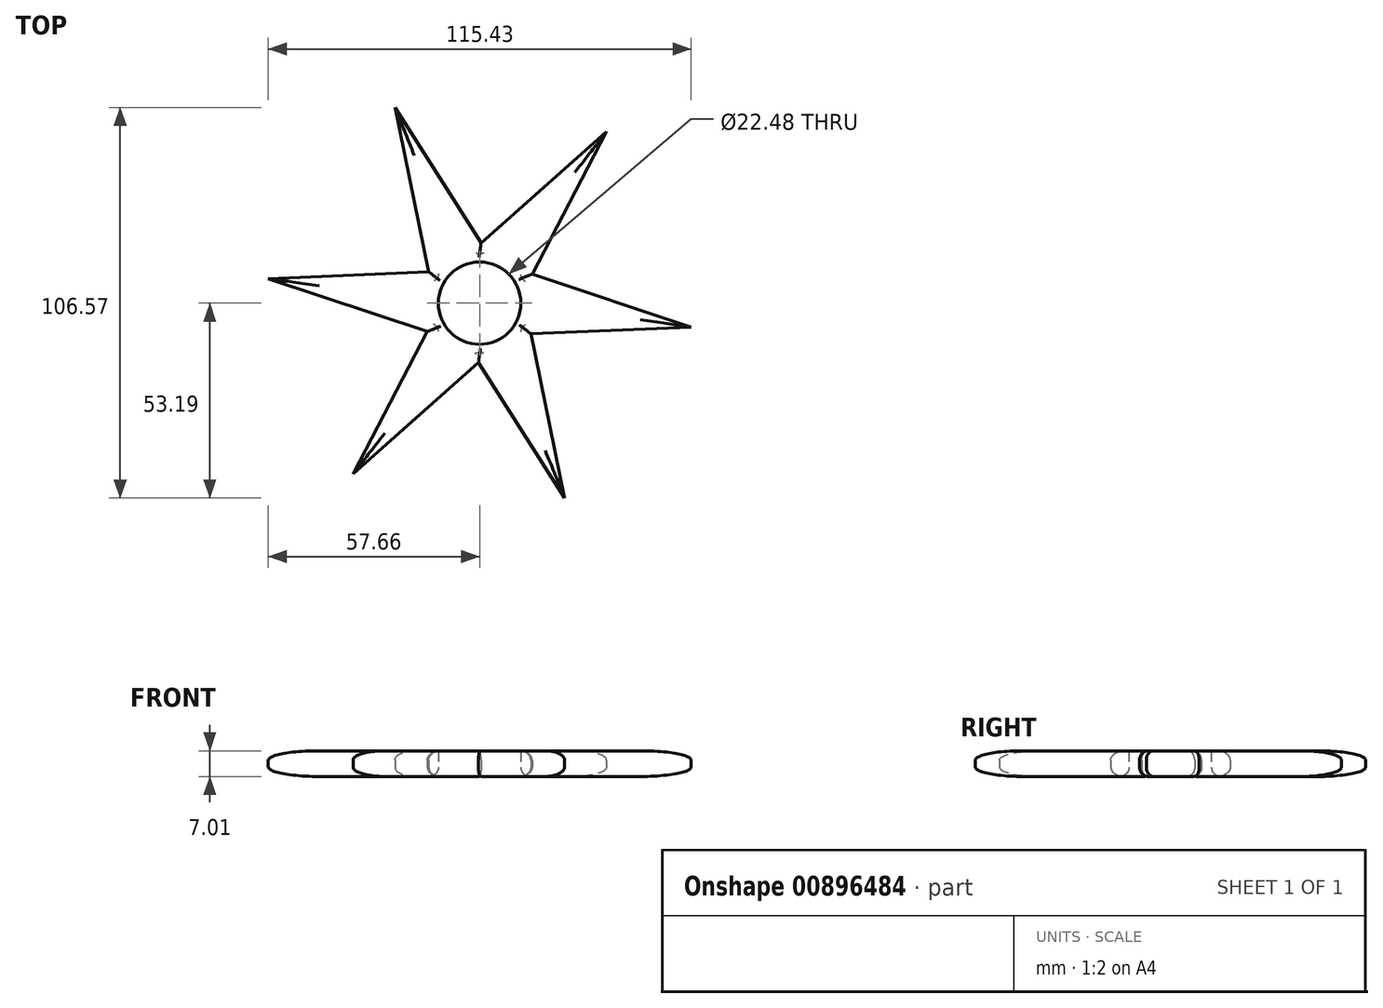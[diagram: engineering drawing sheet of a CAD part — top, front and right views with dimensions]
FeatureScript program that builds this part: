
annotation { "Feature Type Name" : "Feature", "Feature Type Description" : "" }
export const myFeature = defineFeature(function(context is Context, id is Id, definition is map)
    precondition{}
    {
        {
            var Q0;
            Q0=qCreatedBy(makeId("Top.planeOp"),FACE);
            var sketch = newSketch(context, id + "F0", { "sketchPlane" : qUnion([Q0])});
            skCircle(sketch, "E0", {"center": v(0, 0) * mm, "radius": 11.24 * mm});
            skCircle(sketch, "E1", {"center": v(0, 0) * mm, "radius": 16.04 * mm});
            skLineSegment(sketch, "E2", {"start": v(0, 16.04) * mm, "end": v(34.64, 46.77) * mm});
            skLineSegment(sketch, "E3", {"start": v(34.64, 46.77) * mm, "end": v(14.15, 7.54) * mm});
            skLineSegment(sketch, "E4.1.0", {"start": v(-23.08, 53.38) * mm, "end": v(0.66, 16.03) * mm});
            skLineSegment(sketch, "E4.1.1", {"start": v(-13.78, 8.02) * mm, "end": v(-23.08, 53.38) * mm});
            skLineSegment(sketch, "E4.2.0", {"start": v(-57.66, 6.7) * mm, "end": v(-13.44, 8.58) * mm});
            skLineSegment(sketch, "E4.2.1", {"start": v(-13.72, -7.92) * mm, "end": v(-57.66, 6.7) * mm});
            skPoint(sketch, "E4.center", {"position": v(0.05, 0.1) * mm});
            skLineSegment(sketch, "E5.2.3.0", {"start": v(-34.53, -46.58) * mm, "end": v(-14.04, -7.35) * mm});
            skLineSegment(sketch, "E5.3.3.0", {"start": v(0.1, -15.85) * mm, "end": v(-34.53, -46.58) * mm});
            skLineSegment(sketch, "E5.2.4.0", {"start": v(23.2, -53.2) * mm, "end": v(-0.55, -15.84) * mm});
            skLineSegment(sketch, "E5.3.4.0", {"start": v(13.89, -7.83) * mm, "end": v(23.2, -53.2) * mm});
            skLineSegment(sketch, "E5.2.5.0", {"start": v(57.77, -6.51) * mm, "end": v(13.55, -8.4) * mm});
            skLineSegment(sketch, "E5.3.5.0", {"start": v(13.83, 8.11) * mm, "end": v(57.77, -6.51) * mm});
            skSolve(sketch);
        }
        {
            var Q0;
            Q0 = qSketchRegion(id + "F0", true);
            var Q1;
            Q1=makeQuery(id+"F0.imprint","IMPRINT",FACE,{"disambiguationData":[TD([[makeQuery(id+"F0.imprint","IMPRINT",EDGE,{"derivedFrom":sQuery(id+"F0.wireOp",EDGE,"E0")}),-1.0]])]});
            extrude(context, id + "F1", {"entities" : qUnion([Q0, Q1]), "depth" : 7 * mm, "offsetDistance" : 25.4 * mm});
        }
        {
            var Q0;
            Q0=makeQuery(id+"F1.opExtrude","CAP_EDGE",EDGE,{"disambiguationData":[OSD([sQuery(id+"F0.wireOp",EDGE,"E5.3.5.0")])],"isStart":false});
            var Q1;
            Q1=makeQuery(id+"F1.opExtrude","CAP_EDGE",EDGE,{"disambiguationData":[OSD([sQuery(id+"F0.wireOp",EDGE,"E3")])],"isStart":false});
            var Q2;
            Q2=makeQuery(id+"F1.opExtrude","CAP_EDGE",EDGE,{"disambiguationData":[OSD([sQuery(id+"F0.wireOp",EDGE,"E2")])],"isStart":false});
            var Q3;
            Q3=makeQuery(id+"F1.opExtrude","CAP_EDGE",EDGE,{"disambiguationData":[OSD([sQuery(id+"F0.wireOp",EDGE,"E4.1.0")])],"isStart":false});
            var Q4;
            Q4=makeQuery(id+"F1.opExtrude","CAP_EDGE",EDGE,{"disambiguationData":[OSD([sQuery(id+"F0.wireOp",EDGE,"E4.1.1")])],"isStart":false});
            var Q5;
            Q5=makeQuery(id+"F1.opExtrude","CAP_EDGE",EDGE,{"disambiguationData":[OSD([sQuery(id+"F0.wireOp",EDGE,"E4.2.0")])],"isStart":false});
            var Q6;
            Q6=makeQuery(id+"F1.opExtrude","CAP_EDGE",EDGE,{"disambiguationData":[OSD([sQuery(id+"F0.wireOp",EDGE,"E4.2.1")])],"isStart":false});
            var Q7;
            Q7=makeQuery(id+"F1.opExtrude","CAP_EDGE",EDGE,{"disambiguationData":[OSD([sQuery(id+"F0.wireOp",EDGE,"E5.2.3.0")])],"isStart":false});
            var Q8;
            Q8=makeQuery(id+"F1.opExtrude","CAP_EDGE",EDGE,{"disambiguationData":[OSD([sQuery(id+"F0.wireOp",EDGE,"E5.3.3.0")])],"isStart":false});
            var Q9;
            Q9=makeQuery(id+"F1.opExtrude","CAP_EDGE",EDGE,{"disambiguationData":[OSD([sQuery(id+"F0.wireOp",EDGE,"E5.2.4.0")])],"isStart":false});
            var Q10;
            Q10=makeQuery(id+"F1.opExtrude","CAP_EDGE",EDGE,{"disambiguationData":[OSD([sQuery(id+"F0.wireOp",EDGE,"E5.3.4.0")])],"isStart":false});
            var Q11;
            Q11=makeQuery(id+"F1.opExtrude","CAP_EDGE",EDGE,{"disambiguationData":[OSD([sQuery(id+"F0.wireOp",EDGE,"E5.2.5.0")])],"isStart":false});
            fillet(context, id + "F2", {"entities" : qUnion([Q0, Q1, Q2, Q3, Q4, Q5, Q6, Q7, Q8, Q9, Q10, Q11]), "radius" : 2.54 * mm, "tangentPropagation" : true, "allowEdgeOverflow" : false});
        }
        {
            var Q0;
            Q0=makeQuery(id+"F1.opExtrude","CAP_FACE",FACE,{"disambiguationData":[OSD([sQuery(id+"F0.wireOp",EDGE,"E1"),sQuery(id+"F0.wireOp",EDGE,"E2"),sQuery(id+"F0.wireOp",EDGE,"E3"),sQuery(id+"F0.wireOp",EDGE,"E4.1.0"),sQuery(id+"F0.wireOp",EDGE,"E4.1.1"),sQuery(id+"F0.wireOp",EDGE,"E4.2.0"),sQuery(id+"F0.wireOp",EDGE,"E4.2.1"),sQuery(id+"F0.wireOp",EDGE,"E5.2.3.0"),sQuery(id+"F0.wireOp",EDGE,"E5.3.3.0"),sQuery(id+"F0.wireOp",EDGE,"E5.2.4.0"),sQuery(id+"F0.wireOp",EDGE,"E5.3.4.0"),sQuery(id+"F0.wireOp",EDGE,"E5.2.5.0"),sQuery(id+"F0.wireOp",EDGE,"E5.3.5.0")])],"isStart":true});
            fillet(context, id + "F3", {"entities" : qUnion([Q0]), "radius" : 2.54 * mm, "tangentPropagation" : true, "allowEdgeOverflow" : false});
        }
    });
